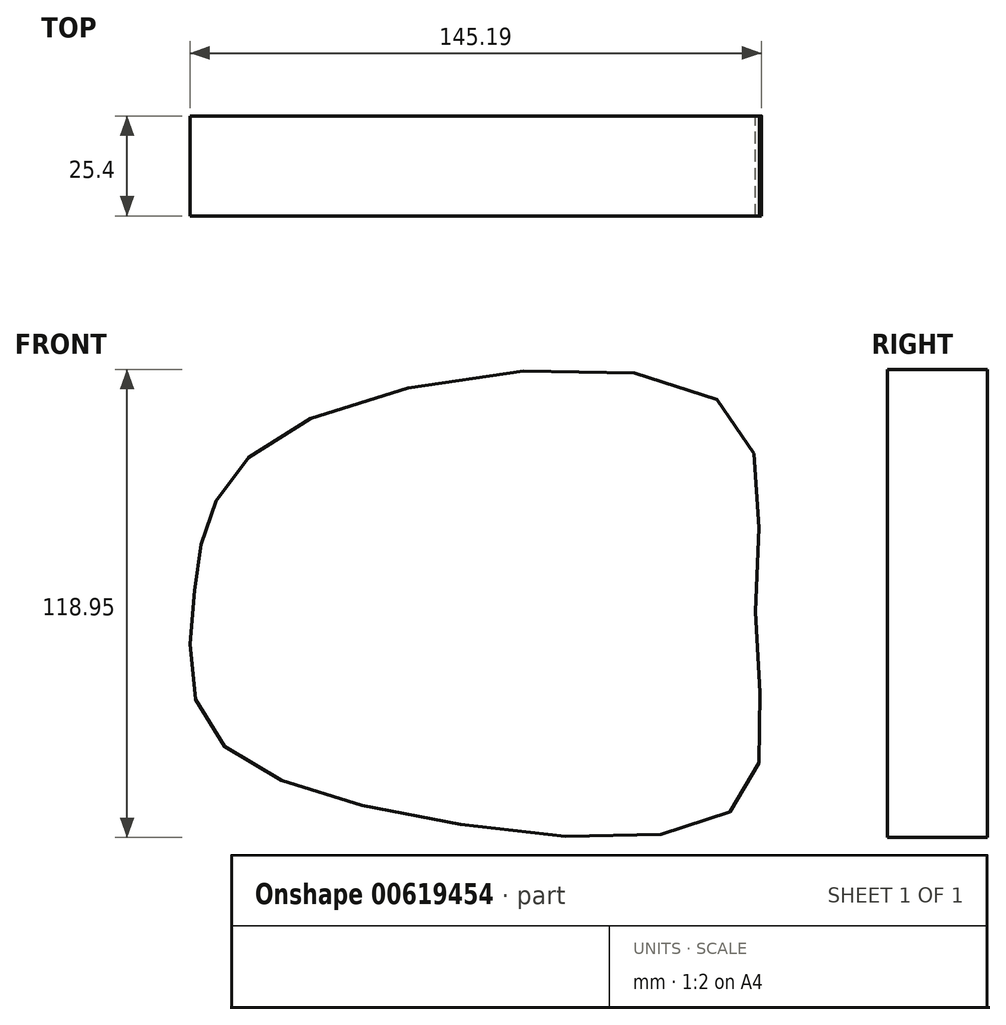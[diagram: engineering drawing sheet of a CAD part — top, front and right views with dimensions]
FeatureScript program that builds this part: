
annotation { "Feature Type Name" : "Feature", "Feature Type Description" : "" }
export const myFeature = defineFeature(function(context is Context, id is Id, definition is map)
    precondition{}
    {
        {
            var Q0;
            Q0=qCreatedBy(makeId("Front.planeOp"),FACE);
            var sketch = newSketch(context, id + "F0", { "sketchPlane" : qUnion([Q0])});
            skFitSpline(sketch, "E0", {"points": [v(-46.73, 59.81) * mm, v(-72.6, 34.4) * mm, v(-76.57, 12.28) * mm, v(-73.07, -18.18) * mm, v(-20.4, -41.2) * mm, v(61.88, -38.43) * mm, v(66.31, 10.17) * mm, v(57.92, 63.69) * mm, v(-46.73, 59.81) * mm]});
            skSolve(sketch);
        }
        {
            var Q0;
            Q0=makeQuery(id+"F0.imprint","IMPRINT",FACE,{"disambiguationData":[TD([[makeQuery(id+"F0.imprint","IMPRINT",EDGE,{"derivedFrom":sQuery(id+"F0.wireOp",EDGE,"E0")}),1.0]])]});
            extrude(context, id + "F1", {"entities" : qUnion([Q0]), "depth" : 25.4 * mm, "offsetDistance" : 25.4 * mm});
        }
    });
